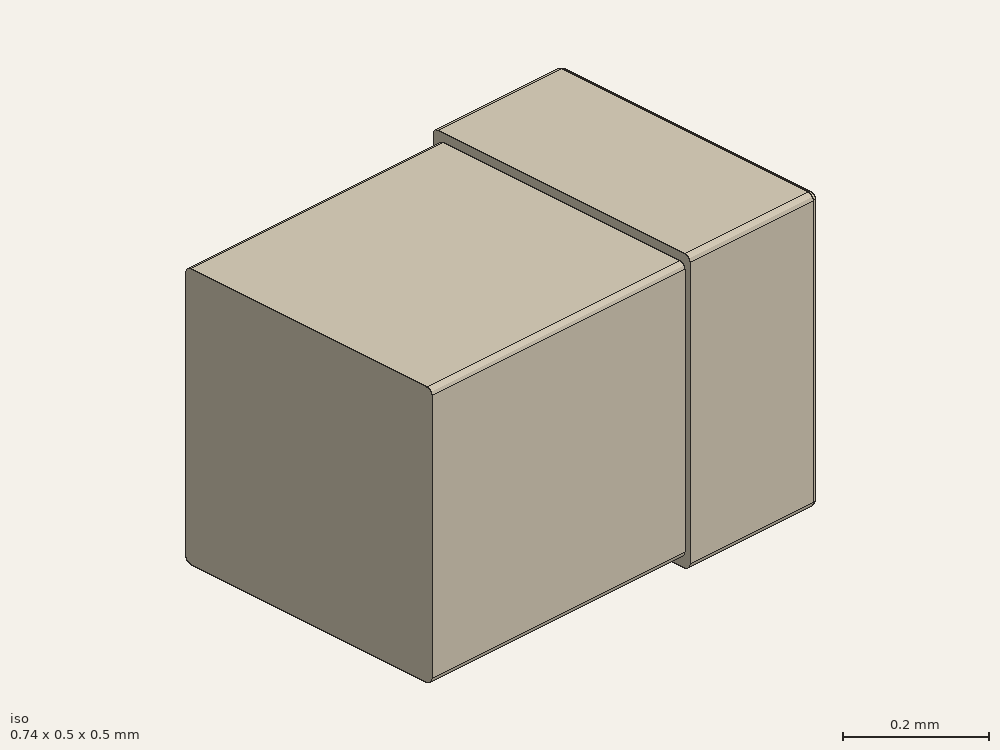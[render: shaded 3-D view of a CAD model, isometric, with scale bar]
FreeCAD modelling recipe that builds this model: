
FCSTD DOCUMENT  (FreeCAD 0.16R6703 (Git))
Label: C_0402
License: All rights reserved
LicenseURL: http://en.wikipedia.org/wiki/All_rights_reserved
objects: Part::Box×2, Part::Fillet×2, Part::FeaturePython×2, App::DocumentObjectGroup×1, Part::Mirroring×1
note: 7 computed .brp shape members not serialized (recipe doc carries the construction recipe); baked Part::Feature solids carry a one-line shape summary decoded from their .brp

FEATURE [Part::Box] Box  label="Cube"
  Height = 0.47
  Length = 0.5
  Placement = pos=(-0.25,-0.24,0.015) rot=(0,0,1;0rad)
  Width = 0.48
FEATURE [Part::Fillet] Fillet  label="body-src"
  Base = -> Box
  Edges = 4 edges r=0.01: [Edge9,Edge10,Edge11,Edge12]
FEATURE [Part::FeaturePython] Clone  label="body"  # Draft clone (typed FeaturePython)
  Objects = -> [Fillet]
  Scale = (1,1,1)
FEATURE [Part::Box] Box001  label="side-src"
  Height = 0.5
  Length = 0.25
  Placement = pos=(-0.4925,-0.25,0) rot=(0,0,1;0rad)
  Width = 0.5
FEATURE [Part::Fillet] Fillet001  label="left-side-src"
  Base = -> Box001
  Edges = 8 edges r=0.01: [Edge1,Edge2,Edge3,Edge4,Edge9,Edge10,Edge11,Edge12]
FEATURE [App::DocumentObjectGroup] Group  label="src"
  Group = -> [Fillet,Box001,Fillet001]
FEATURE [Part::FeaturePython] Clone001  label="left-side"  # Draft clone (typed FeaturePython)
  Objects = -> [Fillet001]
  Scale = (1,1,1)
FEATURE [Part::Mirroring] Part__Mirroring  label="right-side"
  Base = (0,0,0)
  Normal = (1,0,0)
  Source = -> Clone001
